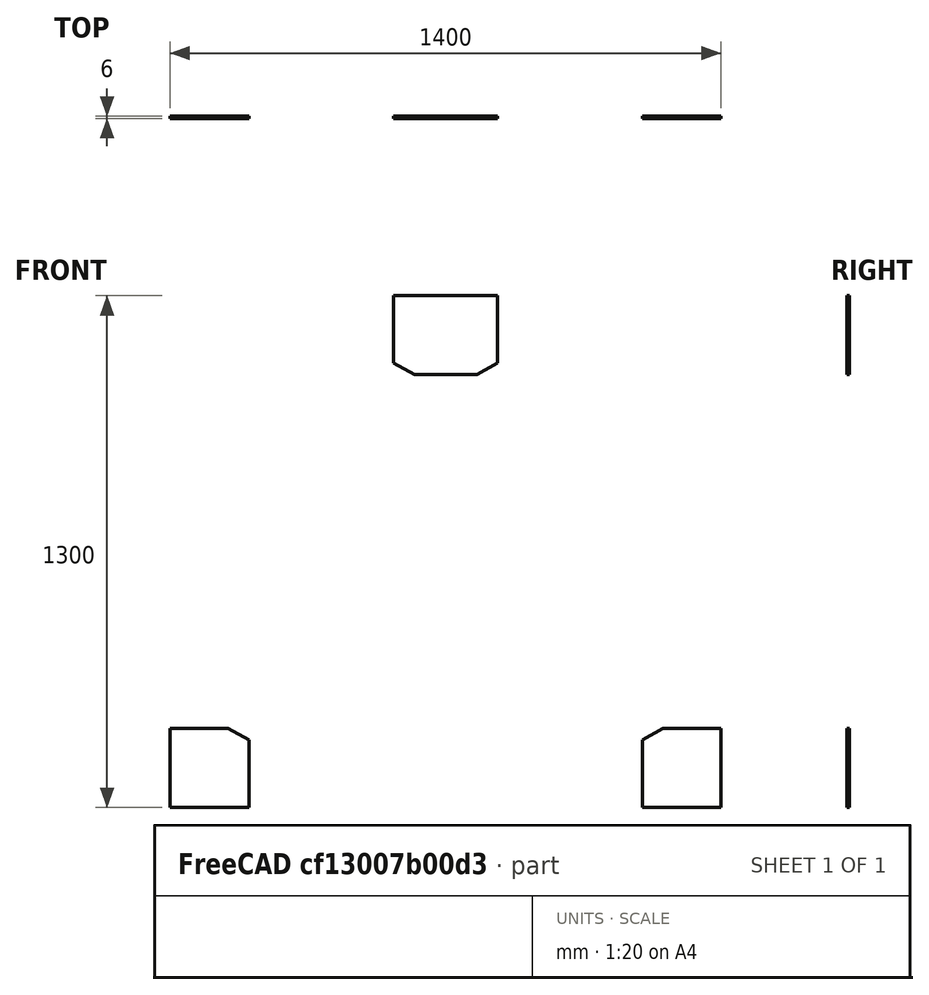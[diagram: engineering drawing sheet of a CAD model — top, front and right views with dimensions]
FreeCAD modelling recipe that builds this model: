
FCSTD DOCUMENT  (FreeCAD 0.21R30492 (Git))
Label: 05_StlFrame01
License: All rights reserved
LicenseURL: http://en.wikipedia.org/wiki/All_rights_reserved
objects: Sketcher::SketchObject×1, Part::Extrusion×1
note: 2 computed .brp shape members not serialized (recipe doc carries the construction recipe); baked Part::Feature solids carry a one-line shape summary decoded from their .brp

FEATURE [Sketcher::SketchObject] Sketch
  FullyConstrained = false
  MapMode = 5
  Placement = pos=(0,0,0) rot=(1,0,0;1.5708rad)
  sketch-geometry (19):
    g0: LineSegment StartX=0 StartY=0 StartZ=0 EndX=200.272 EndY=0 EndZ=0
    g1: LineSegment StartX=200.272 StartY=0 StartZ=0 EndX=200.272 EndY=171.554 EndZ=0
    g2: LineSegment StartX=147.444 StartY=200 StartZ=0 EndX=0 EndY=200 EndZ=0
    g3: LineSegment StartX=0 StartY=200 StartZ=0 EndX=0 EndY=0 EndZ=0
    g4: LineSegment StartX=620.702 StartY=1100 StartZ=0 EndX=779.298 EndY=1100 EndZ=0
    g5: LineSegment StartX=832.127 StartY=1128.45 StartZ=0 EndX=832.127 EndY=1300 EndZ=0
    g6: LineSegment StartX=832.127 StartY=1300 StartZ=0 EndX=567.873 EndY=1300 EndZ=0
    g7: LineSegment StartX=567.873 StartY=1300 StartZ=0 EndX=567.873 EndY=1128.45 EndZ=0
    g8: LineSegment StartX=1199.73 StartY=-1.1e-15 StartZ=0 EndX=1400 EndY=-1.1e-15 EndZ=0
    g9: LineSegment StartX=1400 StartY=-1.1e-15 StartZ=0 EndX=1400 EndY=200 EndZ=0
    g10: LineSegment StartX=1400 StartY=200 StartZ=0 EndX=1252.56 EndY=200 EndZ=0
    g11: LineSegment StartX=1199.73 StartY=171.554 StartZ=0 EndX=1199.73 EndY=0 EndZ=0
    g12: LineSegment StartX=0 StartY=0 StartZ=0 EndX=700 EndY=1300 EndZ=0
    g13: LineSegment StartX=700 StartY=1300 StartZ=0 EndX=1400 EndY=0 EndZ=0
    g14: LineSegment StartX=200.272 StartY=171.554 StartZ=0 EndX=147.444 EndY=200 EndZ=0
    g15: LineSegment StartX=700 StartY=1300 StartZ=0 EndX=700 EndY=-0.683941 EndZ=0
    g16: LineSegment StartX=1199.73 StartY=171.554 StartZ=0 EndX=1252.56 EndY=200 EndZ=0
    g17: LineSegment StartX=620.702 StartY=1100 StartZ=0 EndX=567.873 EndY=1128.45 EndZ=0
    g18: LineSegment StartX=779.298 StartY=1100 StartZ=0 EndX=832.127 EndY=1128.45 EndZ=0
  constraints (52):
    c: Coincident(g0,g1)
    c: Coincident(g2,g3)
    c: Coincident(g3,g0)
    c: Horizontal(g0)
    c: Horizontal(g2)
    c: Vertical(g1)
    c: Vertical(g3)
    c: Coincident(g0,g-1)
    c: Coincident(g5,g6)
    c: Coincident(g6,g7)
    c: Horizontal(g4)
    c: Horizontal(g6)
    c: Vertical(g5)
    c: Vertical(g7)
    c: Coincident(g8,g9)
    c: Coincident(g9,g10)
    c: Coincident(g11,g8)
    c: Horizontal(g8)
    c: Horizontal(g10)
    c: Vertical(g9)
    c: Vertical(g11)
    c: Coincident(g0,g12)
    c: Coincident(g12,g13)
    c: Coincident(g8,g13)
    c: PointOnObject(g12,g6)
    c: Perpendicular(g14,g12)
    c: Coincident(g1,g14)
    c: DistanceX(g0,g8) = 1400  'W'
    c: Coincident(g15,g12)
    c: Symmetric(g0,g8,g15)
    c: Symmetric(g5,g6,g15)
    c: Coincident(g10,g16)
    c: Coincident(g11,g16)
    c: Perpendicular(g16,g13)
    c: Coincident(g4,g17)
    c: Coincident(g7,g17)
    c: Coincident(g4,g18)
    c: Coincident(g5,g18)
    c: Perpendicular(g17,g12)
    c: Perpendicular(g18,g13)
    c: Distance(g7,g12) = 35
    c: Distance(g4,g13) = 25
    c: DistanceY(g0,g6) = 1300  'H'
    c: Horizontal(g2,g9)
    c: Coincident(g14,g2)
    c: Distance(g17) = 60
    c: DistanceY(g3,g3) = 200
    c: Distance(g14) = 60
    c: Distance(g16) = 60
    c: DistanceY(g4,g5) = 200
    c: Distance(g2,g12) = 35
    c: Distance(g10,g13) = 35
FEATURE [Part::Extrusion] Extrude
  Base = -> Sketch
  Dir = (0,-1,2e-16)
  DirMode = 2
  FaceMakerClass = Part::FaceMakerBullseye
  LengthFwd = 6
  LengthRev = 0
  Solid = true
  Symmetric = false
